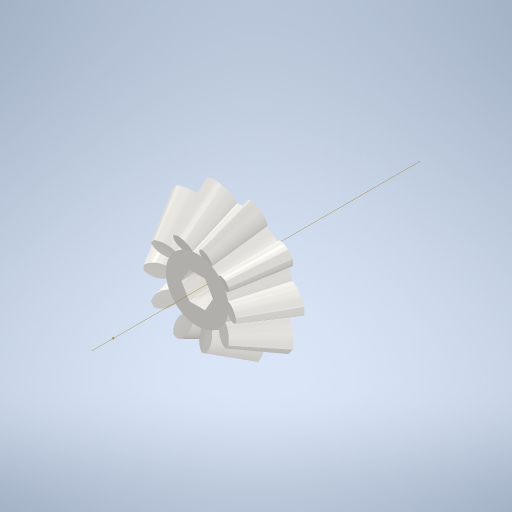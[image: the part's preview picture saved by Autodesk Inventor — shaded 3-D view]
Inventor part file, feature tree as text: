
AUTODESK INVENTOR PART (.ipt)
format: ipt  version: 2024.3 (Build 283343000, 343)  size: 599,552 bytes
history: native  units: mm
features: other x27, loft x2, pattern_circular x2, extrude x1, chamfer x1, fillet x1, sketch x1, reference x1
ambient origin geometry x6: Origin, XZ Plane, X Axis, Y Axis, Z Axis, Center Point
bodies: Solid1 (feature_tree)
feature tree (36):
  other  "Top Point"
  other  "Mesh Plane2"
  other  "Teeth Body"
  other  "Start Point"
  other  "Tooth Plane"
  other  "Start Sketch"
  other  "End Point"
  other  "3D Sketch Right"
  other  "End Plane Right"
  loft  "Loft Right"
  pattern_circular  "Circular Pattern Right"  [2 undecoded]
  other  "3D Sketch Left"
  other  "End Plane Left"
  loft  "Loft Left"
  pattern_circular  "Circular Pattern Left"  [2 undecoded]
  other  "Fix Body"
  extrude  "Extrusion1"  TaperAngle=90.0deg  [1 undecoded]
  chamfer  "Chamfer1"  Distance=2.054002mm
  fillet  "Fillet1"  Radius=2.596628mm
  other  "Mesh Plane"
  other  "Top Plane"
  other  "Teeth Body Sketch"
  other  "End Plane"
  other  "End Sketch"
  other  "Helical Curve Left"
  other  "End Sketch Left"
  other  "Body Sketch"
  other  "Srf1"
  other  "Helical Curve Right"
  other  "End Sketch Right"
  sketch  "Sketch8"  dims[d0=10.0mm d1=7.853375mm d2=11.580644mm d3=4.0mm d4=9.604839mm d5=90.0deg d7=2.054002mm d8=2.596628mm d9=4.55392mm d11=4.10418mm d12=1.3mm d15=1.643434mm d16=2.882226mm d17=0.0mm d18=90.0deg d19=0.0mm d20=90.0deg d21=100.0mm d22=360.0deg d26=63.391752mm d27=3.67089mm d28=10.0mm d29=-4.636476mm d30=1.3mm d31=1.643434mm d32=2.882226mm d35=0.0mm d37=0.0mm d39=0.0mm d40=90.0deg d41=100.0mm d42=360.0deg d46=90.0deg d47=90.0deg d48=0.0mm d49=0.0mm d50=90.0deg d51=3.141593mm d52=0.0mm d53=0.0mm d54=0.0mm d56=3.326736mm d57=7.098859mm d58=4.140137mm d59=4.492945mm d60=2.620338mm d61=4.492945mm d62=2.620338mm d65=63.391752mm d66=31.5mm d67=10.0mm d68=-4.636476mm d69=3.67089mm d70=1.643434mm d71=2.882226mm d72=1.3mm d73=2.620338mm d74=4.492945mm d75=0.0mm d77=0.0mm d79=0.0mm d80=90.0deg d81=100.0mm d82=360.0deg d84=10.0mm d85=20.0mm d86=20.0mm d87=10.0mm d88=0.0mm d89=0.0mm d90=90.0deg d91=90.0deg d92=90.0deg d93=90.0deg d94=0.2mm d95=0.0mm d96=0.0mm d97=0.25mm d98=3.75mm d99=45.0deg d100=0.5mm]
  reference  "Reference1"
  other  "Pitch Diameter"
  other  "<userpath> TUF\Documents\Inventor\ParkinsonDetection\ReductorTrimmer.iam"
  other  "ReductorTrimmer.iam"
  other  "3296W:1"
note: 5 required parameter values undecoded (feature->parameter linkage not recoverable at this tier; creation-order binding heuristic only, values carry confidence <= 0.55)
